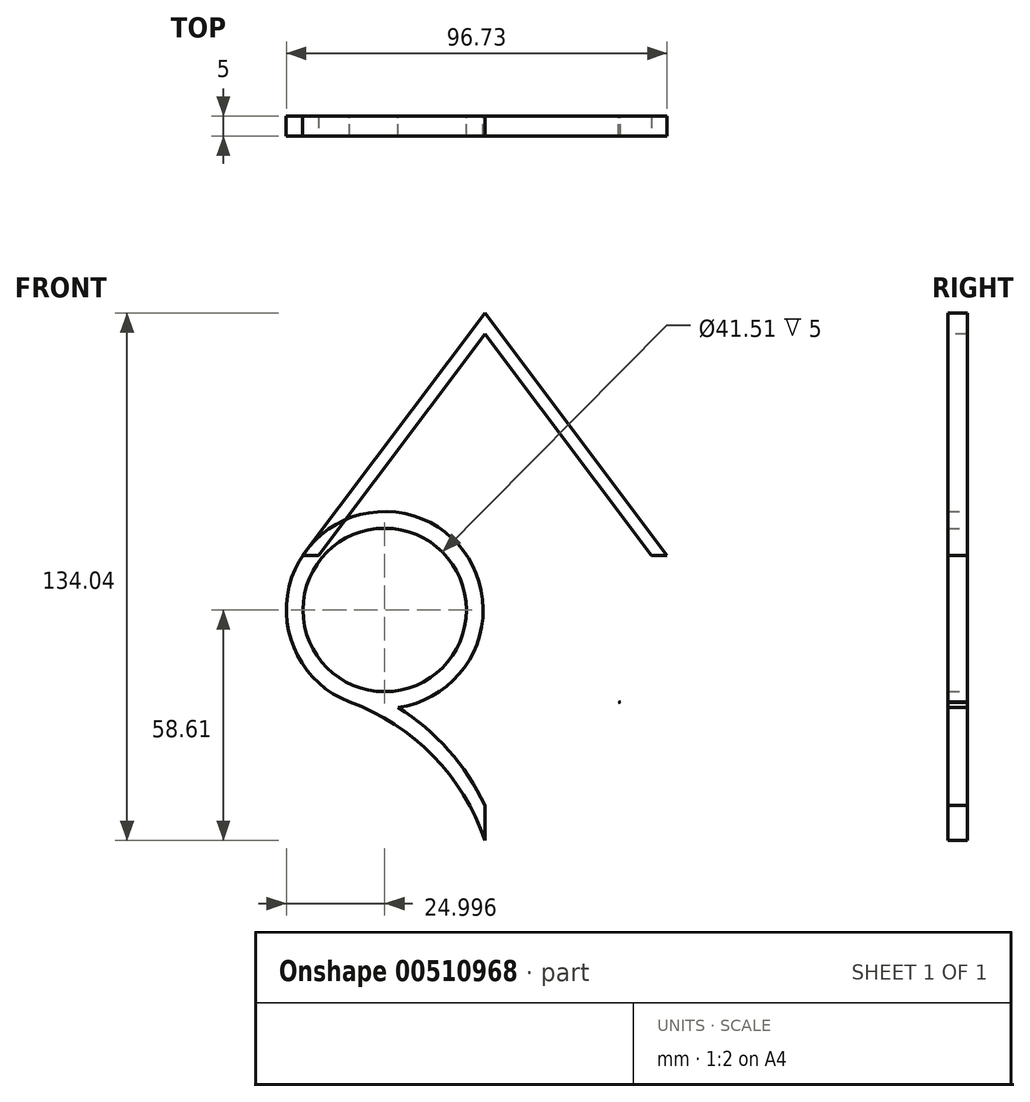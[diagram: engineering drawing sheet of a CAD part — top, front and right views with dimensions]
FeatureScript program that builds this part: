
annotation { "Feature Type Name" : "Feature", "Feature Type Description" : "" }
export const myFeature = defineFeature(function(context is Context, id is Id, definition is map)
    precondition{}
    {
        {
            var Q0;
            Q0=qCreatedBy(makeId("Front.planeOp"),FACE);
            var sketch = newSketch(context, id + "F0", { "sketchPlane" : qUnion([Q0])});
            skCircle(sketch, "E0", {"center": v(-25.45, 0) * mm, "radius": 25 * mm});
            skCircle(sketch, "E1.MirrorC", {"center": v(25.45, 0) * mm, "radius": 25 * mm});
            skLineSegment(sketch, "E2", {"start": v(0, 0) * mm, "end": v(0, -71.84) * mm});
            skArc(sketch, "E3", {"start": v(0, -58.6) * mm, "mid": v(-13.19, -37.06) * mm, "end": v(-34.4, -23.34) * mm});
            skArc(sketch, "E4.MirrorCS", {"start": v(0, -58.6) * mm, "mid": v(13.19, -37.06) * mm, "end": v(34.4, -23.34) * mm});
            skLineSegment(sketch, "E5", {"start": v(0, -4.28) * mm, "end": v(-0.45, 0) * mm});
            skLineSegment(sketch, "E6", {"start": v(0, -4.28) * mm, "end": v(0.45, 0) * mm});
            skCircle(sketch, "E7", {"center": v(-25.45, 0) * mm, "radius": 20.76 * mm});
            skArc(sketch, "E8", {"start": v(0, -49.66) * mm, "mid": v(-13.65, -31.18) * mm, "end": v(-33.27, -19.23) * mm});
            skCircle(sketch, "E9.MirrorC", {"center": v(25.45, 0) * mm, "radius": 20.76 * mm});
            skArc(sketch, "E10", {"start": v(34.4, -18.73) * mm, "mid": v(13.94, -30.56) * mm, "end": v(0, -49.66) * mm});
            skSolve(sketch);
        }
        {
            var Q0;
            {var subQ0=sQuery(id+"F0.wireOp",EDGE,"E3");var subQ1=sQuery(id+"F0.wireOp",EDGE,"E0");var subQ2=makeQuery(id+"F0.imprint","INTERSECT",VERTEX,{"disambiguationData":[OD(0.0)],"derivedFrom":[subQ1,subQ0]});Q0=makeQuery(id+"F0.imprint","IMPRINT",FACE,{"disambiguationData":[TD([[makeQuery(id+"F0.imprint","IMPRINT",EDGE,{"disambiguationData":[TD([[subQ2,1.0]])],"derivedFrom":subQ1}),1.0]])]});}
            var Q1;
            {var subQ0=sQuery(id+"F0.wireOp",EDGE,"E4.MirrorCS");var subQ1=sQuery(id+"F0.wireOp",EDGE,"E1.MirrorC");var subQ2=makeQuery(id+"F0.imprint","INTERSECT",VERTEX,{"disambiguationData":[OD(0.0)],"derivedFrom":[subQ1,subQ0]});Q1=makeQuery(id+"F0.imprint","IMPRINT",FACE,{"disambiguationData":[TD([[makeQuery(id+"F0.imprint","IMPRINT",EDGE,{"disambiguationData":[TD([[subQ2,1.0]])],"derivedFrom":subQ1}),-1.0]])]});}
            var Q2;
            {var subQ0=sQuery(id+"F0.wireOp",EDGE,"E3");var subQ1=sQuery(id+"F0.wireOp",EDGE,"E0");var subQ2=makeQuery(id+"F0.imprint","INTERSECT",VERTEX,{"disambiguationData":[OD(1.0)],"derivedFrom":[subQ1,subQ0]});Q2=makeQuery(id+"F0.imprint","IMPRINT",FACE,{"disambiguationData":[TD([[makeQuery(id+"F0.imprint","IMPRINT",EDGE,{"disambiguationData":[TD([[subQ2,-1.0]])],"derivedFrom":subQ1}),-1.0]])]});}
            var Q3;
            {var subQ0=sQuery(id+"F0.wireOp",EDGE,"E4.MirrorCS");var subQ1=sQuery(id+"F0.wireOp",EDGE,"E1.MirrorC");var subQ2=makeQuery(id+"F0.imprint","INTERSECT",VERTEX,{"disambiguationData":[OD(1.0)],"derivedFrom":[subQ1,subQ0]});Q3=makeQuery(id+"F0.imprint","IMPRINT",FACE,{"disambiguationData":[TD([[makeQuery(id+"F0.imprint","IMPRINT",EDGE,{"disambiguationData":[TD([[subQ2,-1.0]])],"derivedFrom":subQ1}),1.0]])]});}
            extrude(context, id + "F1", {"entities" : qUnion([Q0, Q1, Q2, Q3]), "depth" : 5 * mm, "offsetDistance" : 25 * mm});
        }
        {
            var Q0;
            Q0=makeQuery(id+"F1.opExtrude","CAP_FACE",FACE,{"disambiguationData":[OSD([sQuery(id+"F0.wireOp",EDGE,"E0"),sQuery(id+"F0.wireOp",EDGE,"E1.MirrorC"),sQuery(id+"F0.wireOp",EDGE,"E3"),sQuery(id+"F0.wireOp",EDGE,"E4.MirrorCS"),sQuery(id+"F0.wireOp",EDGE,"E5"),sQuery(id+"F0.wireOp",EDGE,"E6")])],"isStart":false});
            var sketch = newSketch(context, id + "F2", { "sketchPlane" : qUnion([Q0])});
            skLineSegment(sketch, "E11", {"start": v(-46.28, 13.83) * mm, "end": v(0, 75.43) * mm});
            skLineSegment(sketch, "E12.MirrorCS", {"start": v(46.28, 13.83) * mm, "end": v(0, 75.43) * mm});
            skLineSegment(sketch, "E13", {"start": v(-42.28, 13.83) * mm, "end": v(0, 70.1) * mm});
            skLineSegment(sketch, "E14", {"start": v(0, 70.1) * mm, "end": v(42.28, 13.83) * mm});
            skLineSegment(sketch, "E15", {"start": v(-42.28, 13.83) * mm, "end": v(-46.28, 13.83) * mm});
            skLineSegment(sketch, "E16", {"start": v(42.28, 13.83) * mm, "end": v(46.28, 13.83) * mm});
            skSolve(sketch);
        }
        {
            var Q0;
            {var subQ5=sQuery(id+"F2.wireOp",EDGE,"E12.MirrorCS");var subQ6=sQuery(id+"F2.wireOp",EDGE,"E11");var subQ7=makeQuery(id+"F2.imprint","INTERSECT",VERTEX,{"derivedFrom":[subQ6,subQ5]});Q0=makeQuery(id+"F2.imprint","IMPRINT",FACE,{"disambiguationData":[TD([[makeQuery(id+"F2.imprint","IMPRINT",EDGE,{"disambiguationData":[TD([[subQ7,1.0]])],"derivedFrom":subQ6}),-1.0]])]});}
            extrude(context, id + "F3", {"entities" : qUnion([Q0]), "oppositeDirection" : true, "depth" : 5 * mm, "offsetDistance" : 25 * mm});
        }
    });
